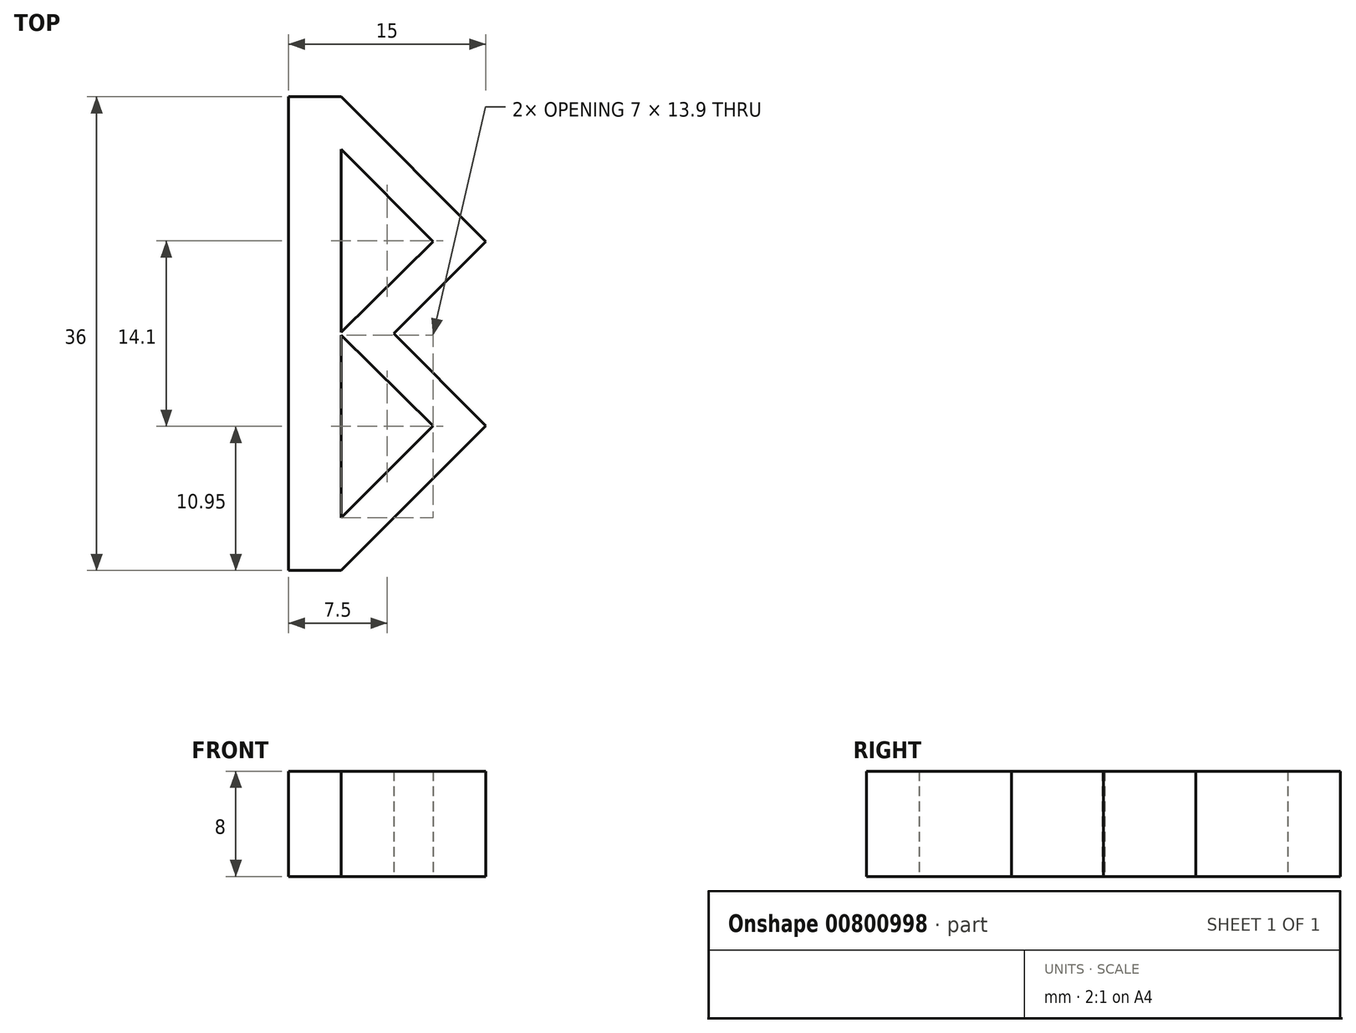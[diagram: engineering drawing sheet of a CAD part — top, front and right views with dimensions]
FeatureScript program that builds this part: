
annotation { "Feature Type Name" : "Feature", "Feature Type Description" : "" }
export const myFeature = defineFeature(function(context is Context, id is Id, definition is map)
    precondition{}
    {
        {
            var Q0;
            Q0=qCreatedBy(makeId("Top.planeOp"),FACE);
            var sketch = newSketch(context, id + "F0", { "sketchPlane" : qUnion([Q0])});
            skLineSegment(sketch, "E0", {"start": v(0, 0) * mm, "end": v(0, -36) * mm});
            skLineSegment(sketch, "E1", {"start": v(0, -36) * mm, "end": v(4, -36) * mm});
            skLineSegment(sketch, "E2", {"start": v(0, 0) * mm, "end": v(4, 0) * mm});
            skLineSegment(sketch, "E3", {"start": v(4, -4) * mm, "end": v(4, -32) * mm});
            skLineSegment(sketch, "E4", {"start": v(4, 0) * mm, "end": v(15, -11) * mm});
            skLineSegment(sketch, "E5", {"start": v(15, -25) * mm, "end": v(4, -36) * mm});
            skLineSegment(sketch, "E6", {"start": v(4, -4) * mm, "end": v(11, -11) * mm});
            skLineSegment(sketch, "E7", {"start": v(15, -11) * mm, "end": v(8.02, -18) * mm});
            skLineSegment(sketch, "E8", {"start": v(8.02, -18) * mm, "end": v(15, -25) * mm});
            skLineSegment(sketch, "E9", {"start": v(4, -32) * mm, "end": v(11, -25) * mm});
            skLineSegment(sketch, "E10", {"start": v(11, -11) * mm, "end": v(15, -11) * mm, "construction": true});
            skLineSegment(sketch, "E11", {"start": v(11, -25) * mm, "end": v(4, -18.1) * mm});
            skLineSegment(sketch, "E12", {"start": v(4, -18.1) * mm, "end": v(4, -17.9) * mm});
            skLineSegment(sketch, "E13", {"start": v(4, -17.9) * mm, "end": v(11, -11) * mm});
            skLineSegment(sketch, "E14", {"start": v(8.02, -18) * mm, "end": v(4, -18) * mm, "construction": true});
            skSolve(sketch);
        }
        {
            var Q0;
            Q0=makeQuery(id+"F0.imprint","IMPRINT",FACE,{"disambiguationData":[TD([[makeQuery(id+"F0.imprint","IMPRINT",EDGE,{"derivedFrom":sQuery(id+"F0.wireOp",EDGE,"E0")}),1.0]])]});
            extrude(context, id + "F1", {"entities" : qUnion([Q0]), "depth" : 8 * mm, "offsetDistance" : 25 * mm});
        }
    });
